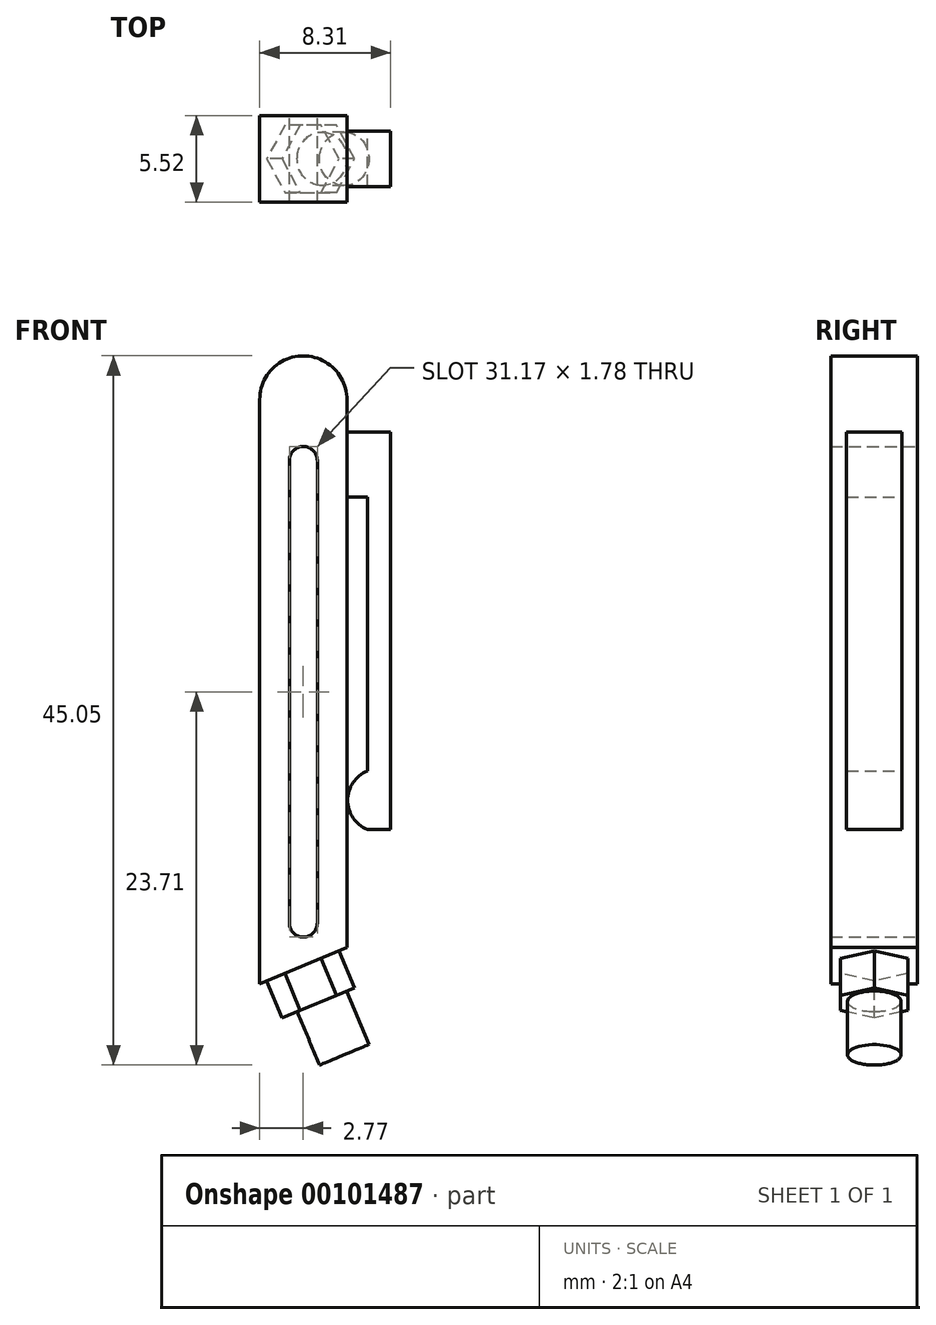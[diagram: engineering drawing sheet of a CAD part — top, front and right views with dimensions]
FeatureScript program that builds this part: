
annotation { "Feature Type Name" : "Feature", "Feature Type Description" : "" }
export const myFeature = defineFeature(function(context is Context, id is Id, definition is map)
    precondition{}
    {
        {
            var Q0;
            Q0=qCreatedBy(makeId("Front.planeOp"),FACE);
            var sketch = newSketch(context, id + "F0", { "sketchPlane" : qUnion([Q0])});
            skLineSegment(sketch, "E0.bottom", {"start": v(2.77, 18.55) * mm, "end": v(-2.77, 18.59) * mm});
            skLineSegment(sketch, "E0.left", {"start": v(2.77, 18.55) * mm, "end": v(2.77, -16.25) * mm});
            skLineSegment(sketch, "E0.right", {"start": v(-2.77, 18.59) * mm, "end": v(-2.77, -18.55) * mm});
            skPoint(sketch, "E0.middle", {"position": v(0, 0) * mm});
            skLineSegment(sketch, "E1.bottom", {"start": v(0.89, 14.7) * mm, "end": v(-0.89, 14.7) * mm});
            skLineSegment(sketch, "E1.top", {"start": v(0.89, -14.7) * mm, "end": v(-0.89, -14.7) * mm});
            skLineSegment(sketch, "E1.left", {"start": v(0.89, 14.7) * mm, "end": v(0.89, -14.7) * mm});
            skLineSegment(sketch, "E1.right", {"start": v(-0.89, 14.7) * mm, "end": v(-0.89, -14.7) * mm});
            skCircle(sketch, "E2", {"center": v(0, 14.7) * mm, "radius": 0.89 * mm});
            skCircle(sketch, "E3.MirrorC", {"center": v(0, -14.7) * mm, "radius": 0.89 * mm});
            skCircle(sketch, "E4", {"center": v(0, 18.57) * mm, "radius": 2.77 * mm});
            skLineSegment(sketch, "E5", {"start": v(-2.77, -18.55) * mm, "end": v(2.77, -16.25) * mm});
            skPoint(sketch, "E0.top.start.orphan", {"position": v(2.77, -18.59) * mm});
            skLineSegment(sketch, "E6.bottom", {"start": v(5.54, 16.5) * mm, "end": v(4.06, 16.5) * mm});
            skLineSegment(sketch, "E6.top", {"start": v(5.54, -8.75) * mm, "end": v(4.06, -8.75) * mm});
            skLineSegment(sketch, "E6.left", {"start": v(5.54, 16.5) * mm, "end": v(5.54, -8.75) * mm});
            skLineSegment(sketch, "E6.right", {"start": v(4.06, 12.36) * mm, "end": v(4.06, -5.03) * mm});
            skPoint(sketch, "E6.middle", {"position": v(4.8, 3.87) * mm});
            skLineSegment(sketch, "E7.bottom", {"start": v(5.54, 16.5) * mm, "end": v(2.77, 16.5) * mm});
            skLineSegment(sketch, "E7.top", {"start": v(4.06, 12.36) * mm, "end": v(2.77, 12.36) * mm});
            skLineSegment(sketch, "E7.left", {"start": v(5.54, 16.5) * mm, "end": v(5.54, 12.36) * mm});
            skLineSegment(sketch, "E7.right", {"start": v(2.77, 16.5) * mm, "end": v(2.77, 12.36) * mm});
            skArc(sketch, "E8", {"start": v(4.06, -5.03) * mm, "mid": v(2.82, -6.89) * mm, "end": v(4.06, -8.75) * mm});
            skSolve(sketch);
        }
        {
            var Q0;
            {var subQ2=sQuery(id+"F0.wireOp",EDGE,"E1.left");Q0=makeQuery(id+"F0.imprint","IMPRINT",FACE,{"disambiguationData":[TD([[makeQuery(id+"F0.imprint","IMPRINT",EDGE,{"derivedFrom":subQ2}),1.0]])]});}
            var Q1;
            {var subQ0=sQuery(id+"F0.wireOp",EDGE,"E4");var subQ1=sQuery(id+"F0.wireOp",EDGE,"E0.bottom");var subQ2=makeQuery(id+"F0.imprint","INTERSECT",VERTEX,{"disambiguationData":[OD(0.0)],"derivedFrom":[subQ1,subQ0]});Q1=makeQuery(id+"F0.imprint","IMPRINT",FACE,{"disambiguationData":[TD([[makeQuery(id+"F0.imprint","IMPRINT",EDGE,{"disambiguationData":[TD([[subQ2,-1.0]])],"derivedFrom":subQ1}),1.0]])]});}
            var Q2;
            {var subQ0=sQuery(id+"F0.wireOp",EDGE,"E4");var subQ1=sQuery(id+"F0.wireOp",EDGE,"E0.bottom");var subQ2=makeQuery(id+"F0.imprint","INTERSECT",VERTEX,{"disambiguationData":[OD(0.0)],"derivedFrom":[subQ1,subQ0]});Q2=makeQuery(id+"F0.imprint","IMPRINT",FACE,{"disambiguationData":[TD([[makeQuery(id+"F0.imprint","IMPRINT",EDGE,{"disambiguationData":[TD([[subQ2,-1.0]])],"derivedFrom":subQ1}),-1.0]])]});}
            extrude(context, id + "F1", {"entities" : qUnion([Q0, Q1, Q2]), "endBound" : BoundingType.SYMMETRIC, "depth" : 5.5 * mm});
        }
        {
            var Q0;
            Q0=qCreatedBy(makeId("Front.planeOp"),FACE);
            var sketch = newSketch(context, id + "F2", { "sketchPlane" : qUnion([Q0])});
            skLineSegment(sketch, "E9.bottom", {"start": v(5.53, 16.5) * mm, "end": v(4.06, 16.5) * mm});
            skLineSegment(sketch, "E9.top", {"start": v(5.53, -8.75) * mm, "end": v(4.06, -8.75) * mm});
            skLineSegment(sketch, "E9.left", {"start": v(5.53, 16.5) * mm, "end": v(5.53, -8.75) * mm});
            skLineSegment(sketch, "E9.right", {"start": v(4.06, 12.36) * mm, "end": v(4.06, -5.03) * mm});
            skLineSegment(sketch, "E10.bottom", {"start": v(5.53, 16.5) * mm, "end": v(2.77, 16.5) * mm});
            skLineSegment(sketch, "E10.top", {"start": v(4.06, 12.36) * mm, "end": v(2.8, 12.36) * mm});
            skArc(sketch, "E11", {"start": v(4.06, -5.03) * mm, "mid": v(2.82, -6.89) * mm, "end": v(4.06, -8.75) * mm});
            skSolve(sketch);
        }
        {
            var Q0;
            Q0 = qSketchRegion(id + "F2", true);
            var Q1;
            Q1=makeQuery(id+"F0.imprint","IMPRINT",FACE,{"disambiguationData":[TD([[makeQuery(id+"F0.imprint","IMPRINT",EDGE,{"derivedFrom":sQuery(id+"F0.wireOp",EDGE,"E6.top")}),-1.0]])]});
            extrude(context, id + "F3", {"entities" : qUnion([Q0, Q1]), "operationType" : NewBodyOperationType.ADD, "endBound" : BoundingType.SYMMETRIC, "depth" : 3.5 * mm});
        }
        {
            var Q0;
            Q0=makeQuery(id+"F1.opExtrude","SWEPT_FACE",FACE,{"disambiguationData":[OSD([sQuery(id+"F0.wireOp",EDGE,"E5")])]});
            var sketch = newSketch(context, id + "F4", { "sketchPlane" : qUnion([Q0])});
            skCircle(sketch, "E12", {"center": v(-6.43, 0) * mm, "radius": 1.7 * mm});
            skSolve(sketch);
        }
        {
            var Q0;
            Q0=makeQuery(id+"F4.imprint","IMPRINT",FACE,{"disambiguationData":[TD([[makeQuery(id+"F4.imprint","IMPRINT",EDGE,{"derivedFrom":sQuery(id+"F4.wireOp",EDGE,"E12")}),1.0]])]});
            extrude(context, id + "F5", {"entities" : qUnion([Q0]), "operationType" : NewBodyOperationType.ADD, "depth" : 6.22 * mm});
        }
        {
            var Q0;
            Q0=makeQuery(id+"F1.opExtrude","SWEPT_FACE",FACE,{"disambiguationData":[OSD([sQuery(id+"F0.wireOp",EDGE,"E5")])]});
            var sketch = newSketch(context, id + "F6", { "sketchPlane" : qUnion([Q0])});
            skCircle(sketch, "E13.cCircle", {"center": v(-6.68, 0) * mm, "radius": 2.15 * mm, "construction": true});
            skLineSegment(sketch, "E13.0", {"start": v(-5.44, 2.15) * mm, "end": v(-4.2, 0) * mm});
            skLineSegment(sketch, "E13.1", {"start": v(-4.2, 0) * mm, "end": v(-5.44, -2.15) * mm});
            skLineSegment(sketch, "E13.2", {"start": v(-5.44, -2.15) * mm, "end": v(-7.93, -2.15) * mm});
            skLineSegment(sketch, "E13.3", {"start": v(-7.93, -2.15) * mm, "end": v(-9.17, 0) * mm});
            skLineSegment(sketch, "E13.4", {"start": v(-9.17, 0) * mm, "end": v(-7.93, 2.15) * mm});
            skLineSegment(sketch, "E13.5", {"start": v(-7.93, 2.15) * mm, "end": v(-5.44, 2.15) * mm});
            skPoint(sketch, "E13.0.midPoint", {"position": v(-4.82, 1.08) * mm});
            skSolve(sketch);
        }
        {
            var Q0;
            Q0=makeQuery(id+"F6.imprint","IMPRINT",FACE,{"disambiguationData":[TD([[makeQuery(id+"F6.imprint","IMPRINT",EDGE,{"derivedFrom":sQuery(id+"F6.wireOp",EDGE,"E13.0")}),-1.0]])]});
            extrude(context, id + "F7", {"entities" : qUnion([Q0]), "operationType" : NewBodyOperationType.ADD, "depth" : 2.54 * mm});
        }
    });
